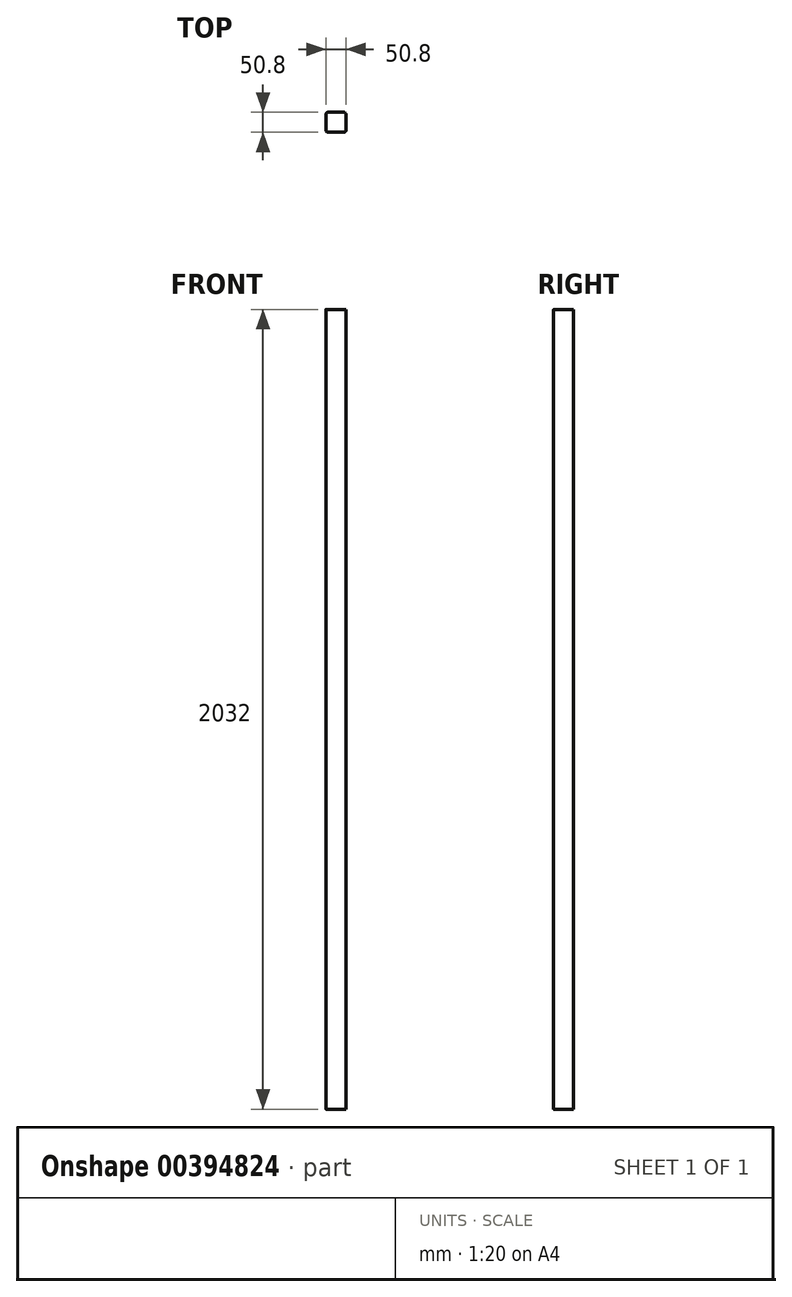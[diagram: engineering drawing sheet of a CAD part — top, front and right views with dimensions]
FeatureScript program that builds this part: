
annotation { "Feature Type Name" : "Feature", "Feature Type Description" : "" }
export const myFeature = defineFeature(function(context is Context, id is Id, definition is map)
    precondition{}
    {
        {
            var Q0;
            Q0=qCreatedBy(makeId("Front.planeOp"),FACE);
            var sketch = newSketch(context, id + "F0", { "sketchPlane" : qUnion([Q0])});
            skLineSegment(sketch, "E0", {"start": v(0, 216.73) * mm, "end": v(0, -403.5) * mm, "construction": true});
            skLineSegment(sketch, "E1", {"start": v(-169.2, 0) * mm, "end": v(472, 0) * mm, "construction": true});
            skLineSegment(sketch, "E2", {"start": v(0, 1016) * mm, "end": v(25.4, 1016) * mm});
            skLineSegment(sketch, "E3", {"start": v(25.4, 1016) * mm, "end": v(25.4, 0) * mm});
            skLineSegment(sketch, "E4.MirrorCS", {"start": v(-25.4, 1016) * mm, "end": v(-25.4, 0) * mm});
            skLineSegment(sketch, "E5.MirrorCS", {"start": v(0, 1016) * mm, "end": v(-25.4, 1016) * mm});
            skLineSegment(sketch, "E6.MirrorCS", {"start": v(-25.4, -1016) * mm, "end": v(-25.4, 0) * mm});
            skLineSegment(sketch, "E7.MirrorCS", {"start": v(25.4, -1016) * mm, "end": v(25.4, 0) * mm});
            skLineSegment(sketch, "E8.MirrorCS", {"start": v(0, -1016) * mm, "end": v(-25.4, -1016) * mm});
            skLineSegment(sketch, "E9.MirrorCS", {"start": v(0, -1016) * mm, "end": v(25.4, -1016) * mm});
            skSolve(sketch);
        }
        {
            var Q0;
            Q0=qSketchRegion(id+"F0",true);
            extrude(context, id + "F1", {"entities" : qUnion([Q0]), "depth" : 50.8 * mm});
        }
        {
            var Q0;
            Q0=makeQuery(id+"F1.opExtrude","CAP_EDGE",EDGE,{"disambiguationData":[OSD([sQuery(id+"F0.wireOp",EDGE,"E3"),sQuery(id+"F0.wireOp",EDGE,"E7.MirrorCS")])],"isStart":false});
            var Q1;
            Q1=makeQuery(id+"F1.opExtrude","CAP_EDGE",EDGE,{"disambiguationData":[OSD([sQuery(id+"F0.wireOp",EDGE,"E3"),sQuery(id+"F0.wireOp",EDGE,"E7.MirrorCS")])],"isStart":true});
            var Q2;
            Q2=makeQuery(id+"F1.opExtrude","CAP_EDGE",EDGE,{"disambiguationData":[OSD([sQuery(id+"F0.wireOp",EDGE,"E4.MirrorCS"),sQuery(id+"F0.wireOp",EDGE,"E6.MirrorCS")])],"isStart":true});
            var Q3;
            Q3=makeQuery(id+"F1.opExtrude","CAP_EDGE",EDGE,{"disambiguationData":[OSD([sQuery(id+"F0.wireOp",EDGE,"E4.MirrorCS"),sQuery(id+"F0.wireOp",EDGE,"E6.MirrorCS")])],"isStart":false});
            fillet(context, id + "F2", {"entities" : qUnion([Q0, Q1, Q2, Q3]), "radius" : 5.08 * mm, "tangentPropagation" : true, "allowEdgeOverflow" : false});
        }
    });
